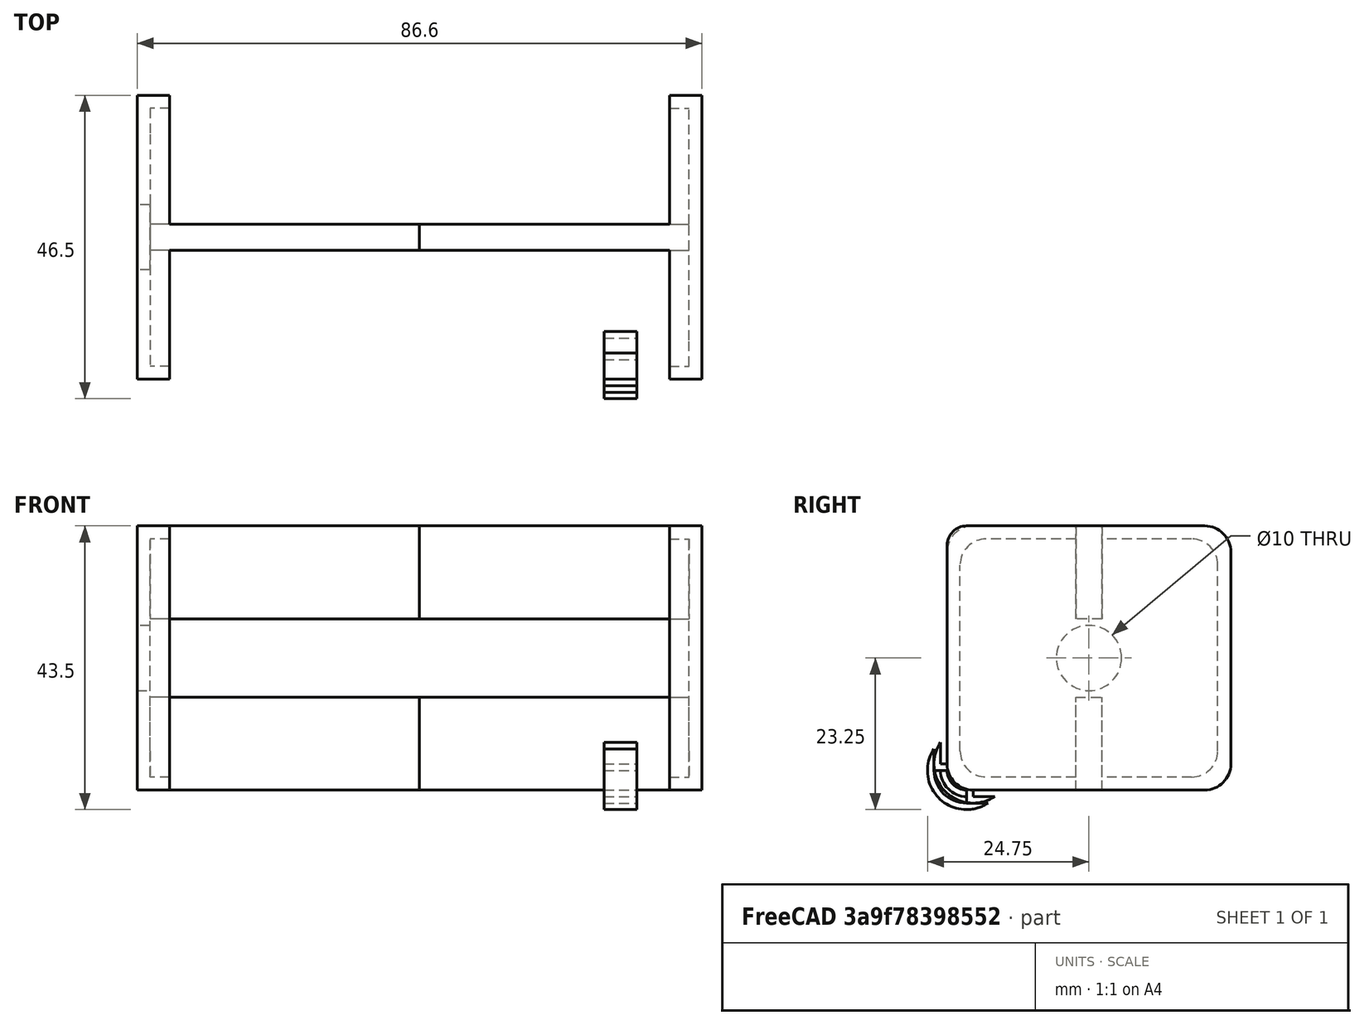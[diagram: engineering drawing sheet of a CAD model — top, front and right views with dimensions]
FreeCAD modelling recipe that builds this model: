
FCSTD DOCUMENT  (FreeCAD 0.21R33771 (Git))
Label: Holder-18650-Adapter-for-TX12
License: All rights reserved
LicenseURL: https://en.wikipedia.org/wiki/All_rights_reserved
objects: Part::Cut×51, Part::Box×40, Part::FeaturePython×16, App::LinkGroup×16, Part::Fuse×4, PartDesign::Body×1, Part::Cylinder×1
note: 113 computed .brp shape members not serialized (recipe doc carries the construction recipe); baked Part::Feature solids carry a one-line shape summary decoded from their .brp

FEATURE [PartDesign::Body] Body
  Origin = -> Origin
FEATURE [Part::Box] Box  label="Cube"
  AttacherType = Attacher::AttachEngine3D
  Height = 40.5
  Length = 5
  Width = 43.5
FEATURE [Part::FeaturePython] Tube  # WARN: FeaturePython — macro-defined, semantics opaque (R4)
  AttacherType = Attacher::AttachEngine3D
  Height = 5
  InnerRadius = 4
  OuterRadius = 6
  Placement = pos=(0,3,3) rot=(0,1,0;1.5708rad)
FEATURE [Part::Box] Box001  label="Cube001"
  AttacherType = Attacher::AttachEngine3D
  Height = 10
  Length = 5
  Placement = pos=(0,3,-2) rot=(0,0,1;0rad)
  Width = 8
FEATURE [Part::Box] Box002  label="Cube002"
  AttacherType = Attacher::AttachEngine3D
  Height = 8
  Length = 5
  Placement = pos=(0,-2,3) rot=(0,0,1;0rad)
  Width = 10
FEATURE [Part::Cut] Cut
  Base = -> Tube
  Tool = -> Box001
FEATURE [Part::Cut] Cut001  label="кут-округлення"
  Base = -> Cut
  Tool = -> Box002
FEATURE [App::LinkGroup] LinkGroup  label="LinkGroup0"
  ElementList = -> [Cut001]
  LinkMode = 0
  Placement = pos=(0,1,1) rot=(0,0,1;0rad)
FEATURE [Part::Box] Box003  label="Cube003"
  AttacherType = Attacher::AttachEngine3D
  Height = 10
  Length = 5
  Placement = pos=(0,3,-2) rot=(0,0,1;0rad)
  Width = 8
FEATURE [Part::Box] Box004  label="Cube004"
  AttacherType = Attacher::AttachEngine3D
  Height = 8
  Length = 5
  Placement = pos=(0,-2,3) rot=(0,0,1;0rad)
  Width = 10
FEATURE [Part::FeaturePython] Tube001  # WARN: FeaturePython — macro-defined, semantics opaque (R4)
  AttacherType = Attacher::AttachEngine3D
  Height = 5
  InnerRadius = 4
  OuterRadius = 6
  Placement = pos=(0,3,3) rot=(0,1,0;1.5708rad)
FEATURE [Part::Cut] Cut002
  Base = -> Tube001
  Tool = -> Box003
FEATURE [Part::Cut] Cut003  label="кут-округлення001"
  Base = -> Cut002
  Tool = -> Box004
FEATURE [App::LinkGroup] LinkGroup001  label="LinkGroup1"
  ElementList = -> [Cut003]
  LinkMode = 0
  Placement = pos=(0,42.5,1) rot=(1,0,0;1.5708rad)
FEATURE [Part::Box] Box005  label="Cube005"
  AttacherType = Attacher::AttachEngine3D
  Height = 10
  Length = 5
  Placement = pos=(0,3,-2) rot=(0,0,1;0rad)
  Width = 8
FEATURE [Part::Box] Box006  label="Cube006"
  AttacherType = Attacher::AttachEngine3D
  Height = 8
  Length = 5
  Placement = pos=(0,-2,3) rot=(0,0,1;0rad)
  Width = 10
FEATURE [Part::FeaturePython] Tube002  # WARN: FeaturePython — macro-defined, semantics opaque (R4)
  AttacherType = Attacher::AttachEngine3D
  Height = 5
  InnerRadius = 4
  OuterRadius = 6
  Placement = pos=(0,3,3) rot=(0,1,0;1.5708rad)
FEATURE [Part::Cut] Cut004
  Base = -> Tube002
  Tool = -> Box005
FEATURE [Part::Cut] Cut005  label="кут-округлення002"
  Base = -> Cut004
  Tool = -> Box006
FEATURE [App::LinkGroup] LinkGroup002  label="LinkGroup2"
  ElementList = -> [Cut005]
  LinkMode = 0
  Placement = pos=(0,42.5,39.5) rot=(1,0,0;3.14159rad)
FEATURE [Part::Box] Box007  label="Cube007"
  AttacherType = Attacher::AttachEngine3D
  Height = 10
  Length = 5
  Placement = pos=(0,3,-2) rot=(0,0,1;0rad)
  Width = 5
FEATURE [Part::Box] Box008  label="Cube008"
  AttacherType = Attacher::AttachEngine3D
  Height = 5
  Length = 5
  Placement = pos=(0,-2,3) rot=(0,0,1;0rad)
  Width = 10
FEATURE [Part::FeaturePython] Tube003  # WARN: FeaturePython — macro-defined, semantics opaque (R4)
  AttacherType = Attacher::AttachEngine3D
  Height = 5
  InnerRadius = 3
  OuterRadius = 5
  Placement = pos=(0,3,3) rot=(0,1,0;1.5708rad)
FEATURE [Part::Cut] Cut006
  Base = -> Tube003
  Tool = -> Box007
FEATURE [Part::Cut] Cut007  label="кут-округлення003"
  Base = -> Cut006
  Tool = -> Box008
FEATURE [App::LinkGroup] LinkGroup003  label="LinkGroup3"
  ElementList = -> [Cut007]
  LinkMode = 0
  Placement = pos=(0,0,40.5) rot=(1,0,0;4.71239rad)
FEATURE [Part::Box] Box009  label="Cube009"
  AttacherType = Attacher::AttachEngine3D
  Height = 10
  Length = 5
  Placement = pos=(0,3,-2) rot=(0,0,1;0rad)
  Width = 8
FEATURE [Part::Box] Box010  label="Cube010"
  AttacherType = Attacher::AttachEngine3D
  Height = 8
  Length = 5
  Placement = pos=(0,-2,3) rot=(0,0,1;0rad)
  Width = 10
FEATURE [Part::FeaturePython] Tube004  # WARN: FeaturePython — macro-defined, semantics opaque (R4)
  AttacherType = Attacher::AttachEngine3D
  Height = 5
  InnerRadius = 4
  OuterRadius = 6
  Placement = pos=(0,3,3) rot=(0,1,0;1.5708rad)
FEATURE [Part::Cut] Cut008
  Base = -> Tube004
  Tool = -> Box009
FEATURE [Part::Cut] Cut009  label="кут-округлення004"
  Base = -> Cut008
  Tool = -> Box010
FEATURE [Part::Box] Box011  label="Cube011"
  AttacherType = Attacher::AttachEngine3D
  Height = 10
  Length = 5
  Placement = pos=(0,3,-2) rot=(0,0,1;0rad)
  Width = 8
FEATURE [Part::Box] Box012  label="Cube012"
  AttacherType = Attacher::AttachEngine3D
  Height = 8
  Length = 5
  Placement = pos=(0,-2,3) rot=(0,0,1;0rad)
  Width = 10
FEATURE [Part::FeaturePython] Tube005  # WARN: FeaturePython — macro-defined, semantics opaque (R4)
  AttacherType = Attacher::AttachEngine3D
  Height = 5
  InnerRadius = 4
  OuterRadius = 6
  Placement = pos=(0,3,3) rot=(0,1,0;1.5708rad)
FEATURE [Part::Cut] Cut010
  Base = -> Tube005
  Tool = -> Box011
FEATURE [Part::Box] Box013  label="Cube013"
  AttacherType = Attacher::AttachEngine3D
  Height = 10
  Length = 5
  Placement = pos=(0,3,-2) rot=(0,0,1;0rad)
  Width = 8
FEATURE [Part::Box] Box014  label="Cube014"
  AttacherType = Attacher::AttachEngine3D
  Height = 8
  Length = 5
  Placement = pos=(0,-2,3) rot=(0,0,1;0rad)
  Width = 10
FEATURE [Part::FeaturePython] Tube006  # WARN: FeaturePython — macro-defined, semantics opaque (R4)
  AttacherType = Attacher::AttachEngine3D
  Height = 5
  InnerRadius = 4
  OuterRadius = 6
  Placement = pos=(0,3,3) rot=(0,1,0;1.5708rad)
FEATURE [Part::Cut] Cut012
  Base = -> Tube006
  Tool = -> Box013
FEATURE [Part::Box] Box015  label="Cube015"
  AttacherType = Attacher::AttachEngine3D
  Height = 10
  Length = 5
  Placement = pos=(0,3,-2) rot=(0,0,1;0rad)
  Width = 8
FEATURE [Part::Box] Box016  label="Cube016"
  AttacherType = Attacher::AttachEngine3D
  Height = 8
  Length = 5
  Placement = pos=(0,-2,3) rot=(0,0,1;0rad)
  Width = 10
FEATURE [Part::FeaturePython] Tube007  # WARN: FeaturePython — macro-defined, semantics opaque (R4)
  AttacherType = Attacher::AttachEngine3D
  Height = 5
  InnerRadius = 4
  OuterRadius = 6
  Placement = pos=(0,3,3) rot=(0,1,0;1.5708rad)
FEATURE [Part::Cut] Cut014
  Base = -> Tube007
  Tool = -> Box015
FEATURE [Part::Cut] Cut016
  Base = -> Box
  Tool = -> LinkGroup
FEATURE [Part::Cut] Cut017
  Base = -> Cut016
  Tool = -> LinkGroup001
FEATURE [Part::Cut] Cut018
  Base = -> Cut017
  Tool = -> LinkGroup002
FEATURE [Part::Cut] Cut019
  Base = -> Cut018
  Tool = -> LinkGroup003
FEATURE [Part::Box] Box017  label="Cube017"
  AttacherType = Attacher::AttachEngine3D
  Height = 36.5
  Length = 3
  Placement = pos=(0,2,2) rot=(0,0,1;0rad)
  Width = 39.5
FEATURE [App::LinkGroup] LinkGroup004  label="LinkGroup4"
  ElementList = -> [Cut009]
  LinkMode = 0
  Placement = pos=(-2,3,3) rot=(0,0,1;0rad)
FEATURE [Part::Cut] Cut011  label="кут-округлення005"
  Base = -> Cut010
  Tool = -> Box012
FEATURE [Part::Cut] Cut013  label="кут-округлення006"
  Base = -> Cut012
  Tool = -> Box014
FEATURE [Part::Cut] Cut015  label="кут-округлення007"
  Base = -> Cut014
  Tool = -> Box016
FEATURE [App::LinkGroup] LinkGroup005  label="LinkGroup5"
  ElementList = -> [Cut011]
  LinkMode = 0
  Placement = pos=(-12,40.5,3) rot=(1,0,0;1.5708rad)
FEATURE [App::LinkGroup] LinkGroup006  label="LinkGroup6"
  ElementList = -> [Cut013]
  LinkMode = 0
  Placement = pos=(-12,3,37.5) rot=(1,0,0;4.71239rad)
FEATURE [App::LinkGroup] LinkGroup007  label="LinkGroup7"
  ElementList = -> [Cut015]
  LinkMode = 0
  Placement = pos=(-12,40.5,37.5) rot=(1,0,0;3.14159rad)
FEATURE [Part::Cut] Cut020
  Base = -> Box017
  Placement = pos=(-10,0,0) rot=(0,0,1;0rad)
  Tool = -> LinkGroup004
FEATURE [Part::Cut] Cut021
  Base = -> Cut020
  Tool = -> LinkGroup005
FEATURE [Part::Cut] Cut022
  Base = -> Cut021
  Tool = -> LinkGroup006
FEATURE [Part::Cut] Cut023
  Base = -> Cut022
  Placement = pos=(10,0,0) rot=(0,0,1;0rad)
  Tool = -> LinkGroup007
FEATURE [Part::Cut] Cut024
  Base = -> Cut019
  Tool = -> Cut023
FEATURE [Part::Box] Box018  label="Cube018"
  AttacherType = Attacher::AttachEngine3D
  Height = 14.25
  Length = 43.3
  Placement = pos=(-38.3,19.75,0) rot=(0,0,1;0rad)
  Width = 4
FEATURE [Part::Box] Box019  label="Cube019"
  AttacherType = Attacher::AttachEngine3D
  Height = 14.25
  Length = 43.3
  Placement = pos=(-38.3,19.75,26.25) rot=(0,0,1;0rad)
  Width = 4
FEATURE [Part::Fuse] Fusion
  Base = -> Cut024
  Tool = -> Box018
FEATURE [Part::Fuse] Fusion001  label="bottom"
  Base = -> Box019
  Placement = pos=(10,0,0) rot=(0,0,1;0rad)
  Tool = -> Fusion
FEATURE [Part::Box] Box020  label="Cube020"
  AttacherType = Attacher::AttachEngine3D
  Height = 40.5
  Length = 5
  Width = 43.5
FEATURE [Part::Box] Box021  label="Cube021"
  AttacherType = Attacher::AttachEngine3D
  Height = 10
  Length = 5
  Placement = pos=(0,3,-2) rot=(0,0,1;0rad)
  Width = 8
FEATURE [Part::Box] Box022  label="Cube022"
  AttacherType = Attacher::AttachEngine3D
  Height = 8
  Length = 5
  Placement = pos=(0,-2,3) rot=(0,0,1;0rad)
  Width = 10
FEATURE [Part::Box] Box023  label="Cube023"
  AttacherType = Attacher::AttachEngine3D
  Height = 10
  Length = 5
  Placement = pos=(0,3,-2) rot=(0,0,1;0rad)
  Width = 8
FEATURE [Part::Box] Box024  label="Cube024"
  AttacherType = Attacher::AttachEngine3D
  Height = 8
  Length = 5
  Placement = pos=(0,-2,3) rot=(0,0,1;0rad)
  Width = 10
FEATURE [Part::Box] Box025  label="Cube025"
  AttacherType = Attacher::AttachEngine3D
  Height = 10
  Length = 5
  Placement = pos=(0,3,-2) rot=(0,0,1;0rad)
  Width = 8
FEATURE [Part::Box] Box026  label="Cube026"
  AttacherType = Attacher::AttachEngine3D
  Height = 8
  Length = 5
  Placement = pos=(0,-2,3) rot=(0,0,1;0rad)
  Width = 10
FEATURE [Part::Box] Box027  label="Cube027"
  AttacherType = Attacher::AttachEngine3D
  Height = 10
  Length = 5
  Placement = pos=(0,3,-2) rot=(0,0,1;0rad)
  Width = 8
FEATURE [Part::Box] Box028  label="Cube028"
  AttacherType = Attacher::AttachEngine3D
  Height = 8
  Length = 5
  Placement = pos=(0,-2,3) rot=(0,0,1;0rad)
  Width = 10
FEATURE [Part::Box] Box029  label="Cube029"
  AttacherType = Attacher::AttachEngine3D
  Height = 10
  Length = 5
  Placement = pos=(0,3,-2) rot=(0,0,1;0rad)
  Width = 8
FEATURE [Part::Box] Box030  label="Cube030"
  AttacherType = Attacher::AttachEngine3D
  Height = 8
  Length = 5
  Placement = pos=(0,-2,3) rot=(0,0,1;0rad)
  Width = 10
FEATURE [Part::Box] Box031  label="Cube031"
  AttacherType = Attacher::AttachEngine3D
  Height = 10
  Length = 5
  Placement = pos=(0,3,-2) rot=(0,0,1;0rad)
  Width = 8
FEATURE [Part::Box] Box032  label="Cube032"
  AttacherType = Attacher::AttachEngine3D
  Height = 8
  Length = 5
  Placement = pos=(0,-2,3) rot=(0,0,1;0rad)
  Width = 10
FEATURE [Part::Box] Box033  label="Cube033"
  AttacherType = Attacher::AttachEngine3D
  Height = 10
  Length = 5
  Placement = pos=(0,3,-2) rot=(0,0,1;0rad)
  Width = 8
FEATURE [Part::Box] Box034  label="Cube034"
  AttacherType = Attacher::AttachEngine3D
  Height = 8
  Length = 5
  Placement = pos=(0,-2,3) rot=(0,0,1;0rad)
  Width = 10
FEATURE [Part::Box] Box035  label="Cube035"
  AttacherType = Attacher::AttachEngine3D
  Height = 10
  Length = 5
  Placement = pos=(0,3,-2) rot=(0,0,1;0rad)
  Width = 8
FEATURE [Part::Box] Box036  label="Cube036"
  AttacherType = Attacher::AttachEngine3D
  Height = 8
  Length = 5
  Placement = pos=(0,-2,3) rot=(0,0,1;0rad)
  Width = 10
FEATURE [Part::Box] Box037  label="Cube037"
  AttacherType = Attacher::AttachEngine3D
  Height = 36.5
  Length = 3
  Placement = pos=(0,2,2) rot=(0,0,1;0rad)
  Width = 39.5
FEATURE [Part::Box] Box038  label="Cube038"
  AttacherType = Attacher::AttachEngine3D
  Height = 14.25
  Length = 43.3
  Placement = pos=(-38.3,19.75,0) rot=(0,0,1;0rad)
  Width = 4
FEATURE [Part::Box] Box039  label="Cube039"
  AttacherType = Attacher::AttachEngine3D
  Height = 14.25
  Length = 43.3
  Placement = pos=(-38.3,19.75,26.25) rot=(0,0,1;0rad)
  Width = 4
FEATURE [Part::FeaturePython] Tube008  # WARN: FeaturePython — macro-defined, semantics opaque (R4)
  AttacherType = Attacher::AttachEngine3D
  Height = 5
  InnerRadius = 4
  OuterRadius = 6
  Placement = pos=(0,3,3) rot=(0,1,0;1.5708rad)
FEATURE [Part::Cut] Cut025
  Base = -> Tube008
  Tool = -> Box021
FEATURE [Part::Cut] Cut026  label="кут-округлення008"
  Base = -> Cut025
  Tool = -> Box022
FEATURE [App::LinkGroup] LinkGroup008
  ElementList = -> [Cut026]
  LinkMode = 0
  Placement = pos=(0,1,1) rot=(0,0,1;0rad)
FEATURE [Part::Cut] Cut041
  Base = -> Box020
  Tool = -> LinkGroup008
FEATURE [Part::FeaturePython] Tube009  # WARN: FeaturePython — macro-defined, semantics opaque (R4)
  AttacherType = Attacher::AttachEngine3D
  Height = 5
  InnerRadius = 4
  OuterRadius = 6
  Placement = pos=(0,3,3) rot=(0,1,0;1.5708rad)
FEATURE [Part::Cut] Cut027
  Base = -> Tube009
  Tool = -> Box023
FEATURE [Part::Cut] Cut028  label="кут-округлення009"
  Base = -> Cut027
  Tool = -> Box024
FEATURE [App::LinkGroup] LinkGroup009
  ElementList = -> [Cut028]
  LinkMode = 0
  Placement = pos=(0,42.5,1) rot=(1,0,0;1.5708rad)
FEATURE [Part::Cut] Cut042
  Base = -> Cut041
  Tool = -> LinkGroup009
FEATURE [Part::FeaturePython] Tube010  # WARN: FeaturePython — macro-defined, semantics opaque (R4)
  AttacherType = Attacher::AttachEngine3D
  Height = 5
  InnerRadius = 4
  OuterRadius = 6
  Placement = pos=(0,3,3) rot=(0,1,0;1.5708rad)
FEATURE [Part::Cut] Cut029
  Base = -> Tube010
  Tool = -> Box025
FEATURE [Part::Cut] Cut030  label="кут-округлення010"
  Base = -> Cut029
  Tool = -> Box026
FEATURE [App::LinkGroup] LinkGroup010
  ElementList = -> [Cut030]
  LinkMode = 0
  Placement = pos=(0,42.5,39.5) rot=(1,0,0;3.14159rad)
FEATURE [Part::Cut] Cut043
  Base = -> Cut042
  Tool = -> LinkGroup010
FEATURE [Part::FeaturePython] Tube011  # WARN: FeaturePython — macro-defined, semantics opaque (R4)
  AttacherType = Attacher::AttachEngine3D
  Height = 5
  InnerRadius = 4
  OuterRadius = 6
  Placement = pos=(0,3,3) rot=(0,1,0;1.5708rad)
FEATURE [Part::Cut] Cut031
  Base = -> Tube011
  Tool = -> Box027
FEATURE [Part::Cut] Cut032  label="кут-округлення011"
  Base = -> Cut031
  Tool = -> Box028
FEATURE [App::LinkGroup] LinkGroup011
  ElementList = -> [Cut032]
  LinkMode = 0
  Placement = pos=(0,1,39.5) rot=(1,0,0;4.71239rad)
FEATURE [Part::Cut] Cut044
  Base = -> Cut043
  Tool = -> LinkGroup011
FEATURE [Part::FeaturePython] Tube012  # WARN: FeaturePython — macro-defined, semantics opaque (R4)
  AttacherType = Attacher::AttachEngine3D
  Height = 5
  InnerRadius = 4
  OuterRadius = 6
  Placement = pos=(0,3,3) rot=(0,1,0;1.5708rad)
FEATURE [Part::Cut] Cut033
  Base = -> Tube012
  Tool = -> Box029
FEATURE [Part::Cut] Cut034  label="кут-округлення012"
  Base = -> Cut033
  Placement = pos=(0,1,1) rot=(0,0,1;0rad)
  Tool = -> Box030
FEATURE [App::LinkGroup] LinkGroup012
  ElementList = -> [Cut034]
  LinkMode = 0
  Placement = pos=(-2,2,2) rot=(0,0,1;0rad)
FEATURE [Part::Cut] Cut045
  Base = -> Box037
  Placement = pos=(-10,0,0) rot=(0,0,1;0rad)
  Tool = -> LinkGroup012
FEATURE [Part::FeaturePython] Tube013  # WARN: FeaturePython — macro-defined, semantics opaque (R4)
  AttacherType = Attacher::AttachEngine3D
  Height = 5
  InnerRadius = 4
  OuterRadius = 6
  Placement = pos=(0,3,3) rot=(0,1,0;1.5708rad)
FEATURE [Part::Cut] Cut035
  Base = -> Tube013
  Tool = -> Box031
FEATURE [Part::Cut] Cut036  label="кут-округлення013"
  Base = -> Cut035
  Tool = -> Box032
FEATURE [App::LinkGroup] LinkGroup013
  ElementList = -> [Cut036]
  LinkMode = 0
  Placement = pos=(-12,40.5,3) rot=(1,0,0;1.5708rad)
FEATURE [Part::Cut] Cut046
  Base = -> Cut045
  Tool = -> LinkGroup013
FEATURE [Part::FeaturePython] Tube014  # WARN: FeaturePython — macro-defined, semantics opaque (R4)
  AttacherType = Attacher::AttachEngine3D
  Height = 5
  InnerRadius = 4
  OuterRadius = 6
  Placement = pos=(0,3,3) rot=(0,1,0;1.5708rad)
FEATURE [Part::Cut] Cut037
  Base = -> Tube014
  Tool = -> Box033
FEATURE [Part::Cut] Cut038  label="кут-округлення014"
  Base = -> Cut037
  Tool = -> Box034
FEATURE [App::LinkGroup] LinkGroup014
  ElementList = -> [Cut038]
  LinkMode = 0
  Placement = pos=(-12,3,37.5) rot=(1,0,0;4.71239rad)
FEATURE [Part::Cut] Cut047
  Base = -> Cut046
  Tool = -> LinkGroup014
FEATURE [Part::FeaturePython] Tube015  # WARN: FeaturePython — macro-defined, semantics opaque (R4)
  AttacherType = Attacher::AttachEngine3D
  Height = 5
  InnerRadius = 4
  OuterRadius = 6
  Placement = pos=(0,3,3) rot=(0,1,0;1.5708rad)
FEATURE [Part::Cut] Cut039
  Base = -> Tube015
  Tool = -> Box035
FEATURE [Part::Cut] Cut040  label="кут-округлення015"
  Base = -> Cut039
  Placement = pos=(0,1,1) rot=(0,0,1;0rad)
  Tool = -> Box036
FEATURE [App::LinkGroup] LinkGroup015
  ElementList = -> [Cut040]
  LinkMode = 0
  Placement = pos=(-12,41.5,38.5) rot=(1,0,0;3.14159rad)
FEATURE [Part::Cut] Cut048
  Base = -> Cut047
  Placement = pos=(10,0,0) rot=(0,0,1;0rad)
  Tool = -> LinkGroup015
FEATURE [Part::Cut] Cut049
  Base = -> Cut044
  Tool = -> Cut048
FEATURE [Part::Fuse] Fusion002
  Base = -> Cut049
  Tool = -> Box038
FEATURE [Part::Fuse] Fusion003  label="top-without-hole"
  Base = -> Box039
  Placement = pos=(-66.6,43.5,0) rot=(0,0,1;3.14159rad)
  Tool = -> Fusion002
FEATURE [Part::Cylinder] Cylinder
  Angle = 360
  AttacherType = Attacher::AttachEngine3D
  FirstAngle = 0
  Height = 2
  Placement = pos=(-71.6,21.75,20.25) rot=(0,1,0;1.5708rad)
  Radius = 5
  SecondAngle = 0
FEATURE [Part::Cut] Cut050  label="top"
  Base = -> Fusion003
  Tool = -> Cylinder
